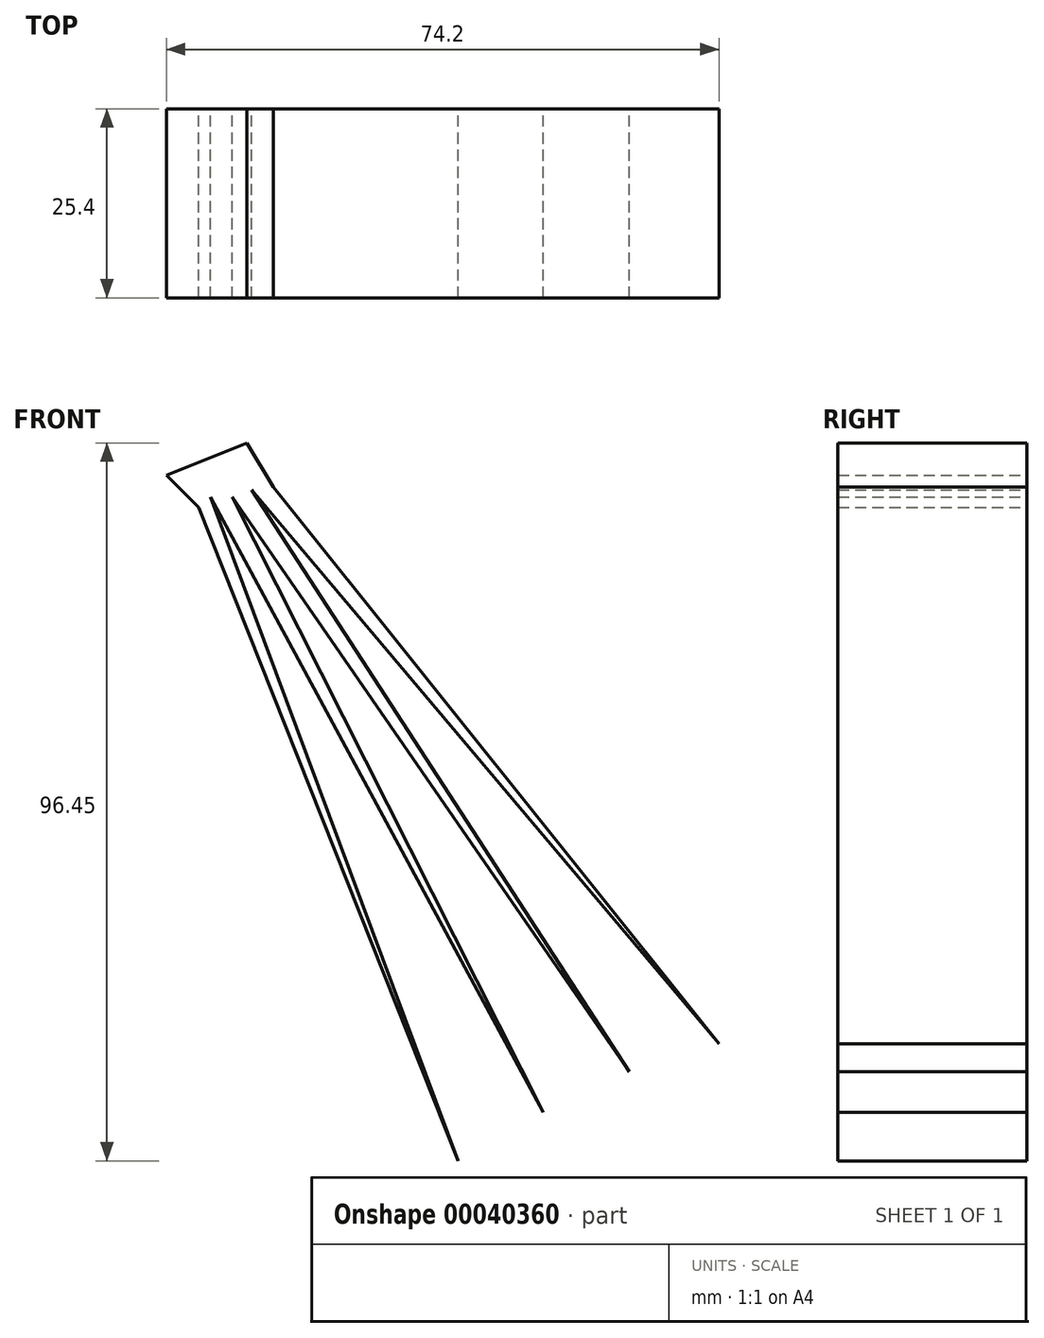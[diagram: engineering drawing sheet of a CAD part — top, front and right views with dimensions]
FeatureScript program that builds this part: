
annotation { "Feature Type Name" : "Feature", "Feature Type Description" : "" }
export const myFeature = defineFeature(function(context is Context, id is Id, definition is map)
    precondition{}
    {
        {
            var Q0;
            Q0=qCreatedBy(makeId("Front.planeOp"),FACE);
            var sketch = newSketch(context, id + "F0", { "sketchPlane" : qUnion([Q0])});
            skLineSegment(sketch, "E0", {"start": v(-54.52, 53.04) * mm, "end": v(-19.68, -34.74) * mm});
            skLineSegment(sketch, "E1", {"start": v(-19.68, -34.74) * mm, "end": v(-52.95, 54.42) * mm});
            skLineSegment(sketch, "E2", {"start": v(-52.95, 54.42) * mm, "end": v(-8.27, -28.24) * mm});
            skLineSegment(sketch, "E3", {"start": v(-8.27, -28.24) * mm, "end": v(-50, 54.42) * mm});
            skLineSegment(sketch, "E4", {"start": v(-50, 54.42) * mm, "end": v(3.35, -22.73) * mm});
            skLineSegment(sketch, "E5", {"start": v(3.35, -22.73) * mm, "end": v(-47.44, 55.4) * mm});
            skLineSegment(sketch, "E6", {"start": v(-47.44, 55.4) * mm, "end": v(15.35, -19) * mm});
            skLineSegment(sketch, "E7", {"start": v(15.35, -19) * mm, "end": v(-44.48, 55.8) * mm});
            skLineSegment(sketch, "E8", {"start": v(-44.48, 55.8) * mm, "end": v(-48.03, 61.7) * mm});
            skLineSegment(sketch, "E9", {"start": v(-48.03, 61.7) * mm, "end": v(-58.85, 57.37) * mm});
            skLineSegment(sketch, "E10", {"start": v(-58.85, 57.37) * mm, "end": v(-54.52, 53.04) * mm});
            skSolve(sketch);
        }
        {
            var Q0;
            Q0=makeQuery(id+"F0.imprint","IMPRINT",FACE,{"disambiguationData":[TD([[makeQuery(id+"F0.imprint","IMPRINT",EDGE,{"derivedFrom":sQuery(id+"F0.wireOp",EDGE,"E0")}),1.0]])]});
            extrude(context, id + "F1", {"entities" : qUnion([Q0]), "depth" : 25.4 * mm});
        }
    });
